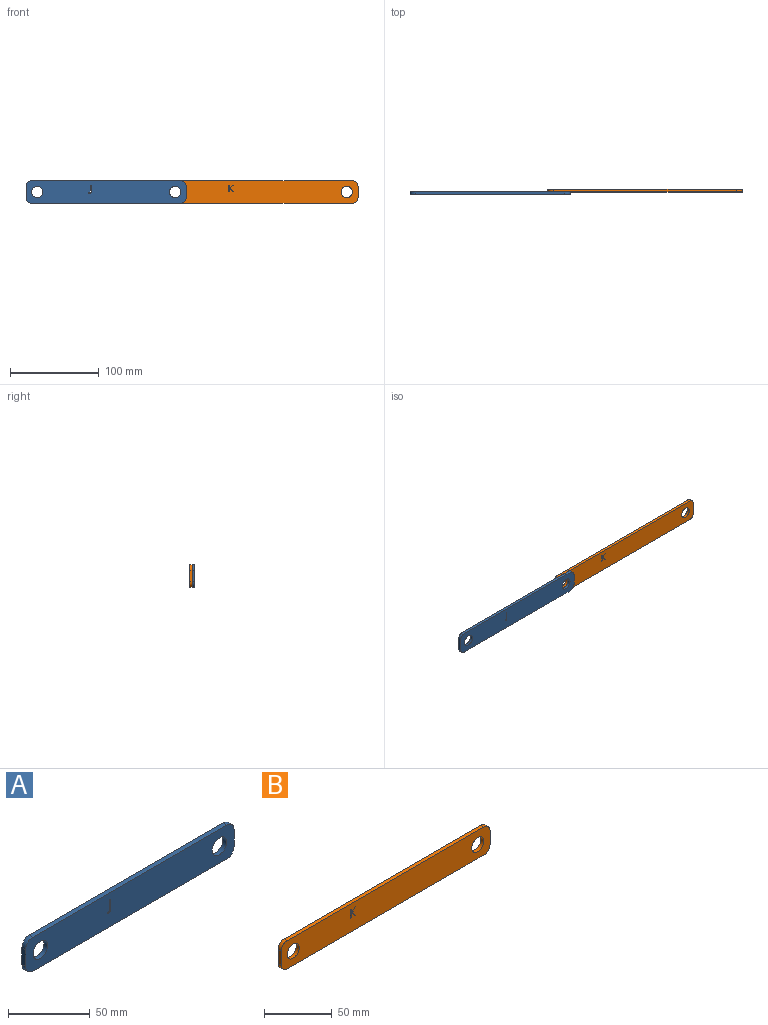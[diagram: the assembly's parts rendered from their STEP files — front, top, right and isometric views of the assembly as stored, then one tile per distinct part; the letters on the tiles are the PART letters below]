
ASSEMBLY  parts=2 mates=1
PART A: 22 faces, bbox 180.3x3.2x25.4 mm
  f0: extruded ~3.18x1.55mm, area 5.3mm2, adj f1,f19,f20,f21
  f1: extruded ~3.18x1.45mm, area 5.1mm2, adj f0,f2,f20,f21
  f2: extruded ~3.18x0.78mm, area 2.5mm2, adj f1,f3,f20,f21
  f3: plane 3.18x0.76mm, normal (1,0,0), area 2.4mm2, adj f2,f4,f20,f21
  f4: extruded ~3.18x0.78mm, area 2.5mm2, adj f3,f5,f20,f21
  f5: extruded ~3.18x0.79mm, area 2.8mm2, adj f4,f6,f20,f21
  f6: extruded ~3.18x0.91mm, area 3.1mm2, adj f5,f7,f20,f21
  f7: plane 7.67x3.18mm, normal (1,0,0), area 24.3mm2, adj f6,f8,f20,f21
  f8: plane 3.18x0.89mm, normal (0,0,-1), area 2.8mm2, adj f7,f19,f20,f21
  f9: cylinder r=6.35mm len=6.35mm, axis (0,1,0), area 31.7mm2, adj f10,f16,f20,f21
  f10: plane 167.64x3.18mm, normal (0,0,-1), area 532.3mm2, adj f9,f11,f20,f21
  f11: cylinder r=6.35mm len=6.35mm, axis (0,1,0), area 31.7mm2, adj f10,f12,f20,f21
  f12: plane 12.7x3.18mm, normal (1,0,0), area 40.3mm2, adj f11,f13,f20,f21
  f13: cylinder r=6.35mm len=6.35mm, axis (0,1,0), area 31.7mm2, adj f12,f14,f20,f21
  f14: plane 167.64x3.18mm, normal (0,0,1), area 532.3mm2, adj f13,f15,f20,f21
  f15: cylinder r=6.35mm len=6.35mm, axis (0,1,0), area 31.7mm2, adj f14,f16,f20,f21
  f16: plane 12.7x3.18mm, normal (-1,0,0), area 40.3mm2, adj f9,f15,f20,f21
  f17: cylinder r=6.35mm len=12.7mm, axis (0,1,0), area 126.7mm2, adj f20,f21
  f18: cylinder r=6.35mm len=12.7mm, axis (0,1,0), area 126.7mm2, adj f20,f21
  f19: plane 7.6x3.18mm, normal (-1,0,0), area 24.1mm2, adj f0,f8,f20,f21
  f20: plane 180.34x25.4mm, normal (0,-1,0), area 4283.1mm2, adj f0,f1,f2,f3,f4,f5,f6,f7
  f21: plane 180.34x25.4mm, normal (0,1,0), area 4283.1mm2, adj f0,f1,f2,f3,f4,f5,f6,f7
PART B: 24 faces, bbox 218.4x3.2x25.4 mm
  f0: plane 3.33x3.18mm, normal (-0.73,0,0.68), area 14.4mm2, adj f1,f21,f22,f23
  f1: plane 4.34x3.2mm, normal (-0.8,0,-0.59), area 17.1mm2, adj f0,f2,f22,f23
  f2: plane 3.18x1.05mm, normal (0,0,1), area 3.3mm2, adj f1,f3,f22,f23
  f3: plane 3.72x3.18mm, normal (0.8,0,0.6), area 14.8mm2, adj f2,f4,f22,f23
  f4: plane 3.18x0.8mm, normal (-0.66,0,0.75), area 3.4mm2, adj f3,f5,f22,f23
  f5: plane 3.18x3.01mm, normal (-1,0,0), area 9.5mm2, adj f4,f6,f22,f23
  f6: plane 3.18x0.89mm, normal (0,0,1), area 2.8mm2, adj f5,f7,f22,f23
  f7: plane 7.67x3.18mm, normal (1,0,0), area 24.3mm2, adj f6,f8,f22,f23
  f8: plane 3.18x0.89mm, normal (0,0,-1), area 2.8mm2, adj f7,f9,f22,f23
  f9: plane 3.8x3.18mm, normal (-1,0,0), area 12.1mm2, adj f8,f10,f22,f23
  f10: plane 3.8x3.48mm, normal (0.74,0,-0.67), area 16.4mm2, adj f9,f21,f22,f23
  f11: cylinder r=6.35mm len=6.35mm, axis (0,1,0), area 31.7mm2, adj f12,f18,f22,f23
  f12: plane 205.74x3.18mm, normal (0,0,-1), area 653.2mm2, adj f11,f13,f22,f23
  f13: cylinder r=6.35mm len=6.35mm, axis (0,1,0), area 31.7mm2, adj f12,f14,f22,f23
  f14: plane 12.7x3.18mm, normal (1,0,0), area 40.3mm2, adj f13,f15,f22,f23
  f15: cylinder r=6.35mm len=6.35mm, axis (0,1,0), area 31.7mm2, adj f14,f16,f22,f23
  f16: plane 205.74x3.18mm, normal (0,0,1), area 653.2mm2, adj f15,f17,f22,f23
  f17: cylinder r=6.35mm len=6.35mm, axis (0,1,0), area 31.7mm2, adj f16,f18,f22,f23
  f18: plane 12.7x3.18mm, normal (-1,0,0), area 40.3mm2, adj f11,f17,f22,f23
  f19: cylinder r=6.35mm len=12.7mm, axis (0,1,0), area 126.7mm2, adj f22,f23
  f20: cylinder r=6.35mm len=12.7mm, axis (0,1,0), area 126.7mm2, adj f22,f23
  f21: plane 3.18x1.05mm, normal (0,0,-1), area 3.3mm2, adj f0,f10,f22,f23
  f22: plane 218.44x25.4mm, normal (0,-1,0), area 5244.9mm2, adj f0,f1,f2,f3,f4,f5,f6,f7
  f23: plane 218.44x25.4mm, normal (0,1,0), area 5244.9mm2, adj f0,f1,f2,f3,f4,f5,f6,f7
PLACE A rot(axis=(0,1,0),0deg) t=(78.55,-12.36,76.01)mm
PLACE B t=(172.58,-9.18,-24.03)mm fixed
MATE revolute B.f19 <-> A.f18  axis (0,-1,0) through (68.76,-12.36,-13.38)mm
